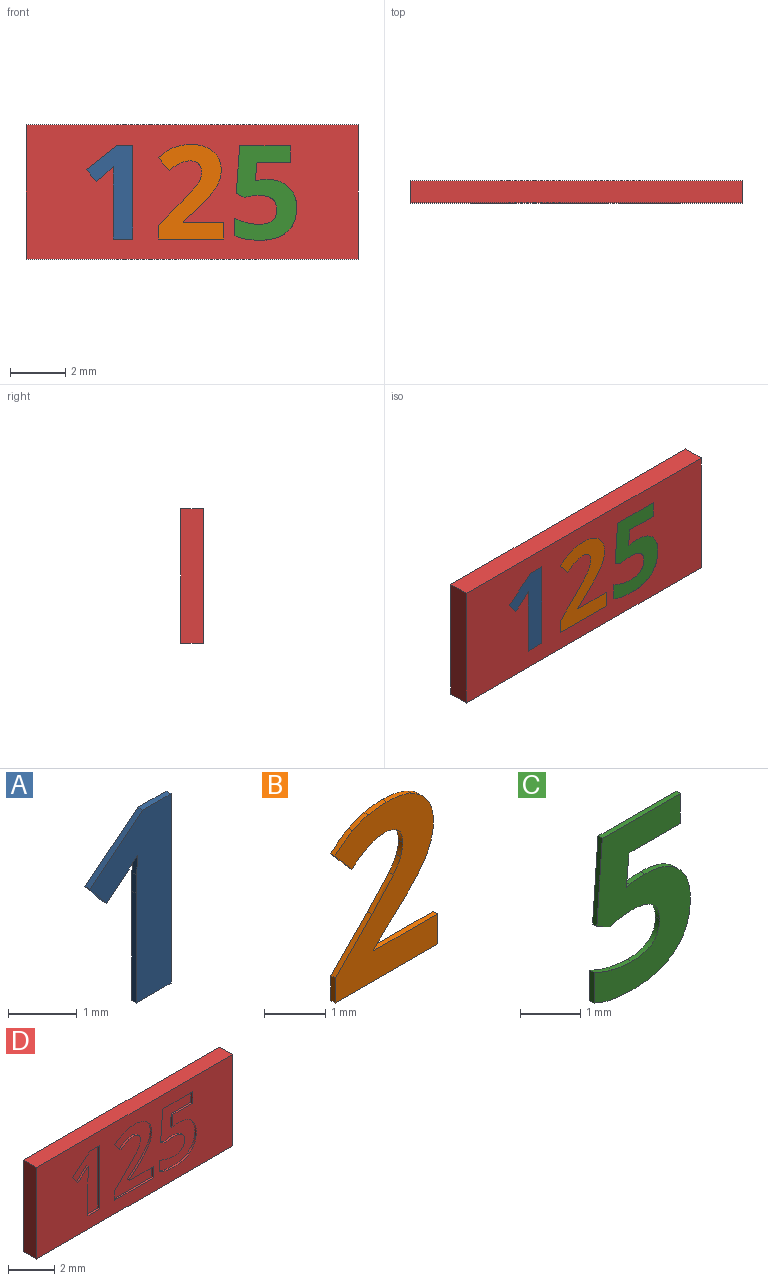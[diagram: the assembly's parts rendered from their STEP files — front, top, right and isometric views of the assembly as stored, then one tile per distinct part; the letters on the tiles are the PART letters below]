
ASSEMBLY  parts=4 mates=3
PART A: 12 faces, bbox 1.7x0.1x3.4 mm
  f0: plane 3.37x1.67mm, normal (0,-1,0), area 2.9mm2, adj f1,f2,f3,f4,f5,f6,f7,f9
  f1: plane 0.59x0.1mm, normal (0,0,1), area 0.1mm2, adj f0,f2,f8,f10
  f2: plane 1.09x0.86mm, normal (-0.62,0,0.78), area 0.1mm2, adj f0,f1,f3,f8
  f3: plane 0.43x0.34mm, normal (-0.78,0,-0.63), area 0.1mm2, adj f0,f2,f4,f8
  f4: plane 0.39x0.31mm, normal (0.63,0,-0.78), area 0mm2, adj f0,f3,f5,f8
  f5: extruded ~0.25x0.23mm, area 0mm2, adj f0,f4,f6,f8
  f6: plane 0.35x0.1mm, normal (-1,0,0.03), area 0mm2, adj f0,f5,f7,f8
  f7: plane 0.32x0.1mm, normal (-1,0,0.02), area 0mm2, adj f0,f6,f8,f9
  f8: plane 3.37x1.67mm, normal (0,1,0), area 2.9mm2, adj f1,f2,f3,f4,f5,f6,f7,f9
  f9: plane 1.95x0.1mm, normal (-1,0,0), area 0.2mm2, adj f0,f7,f8,f11
  f10: plane 3.37x0.1mm, normal (1,0,0), area 0.3mm2, adj f0,f1,f8,f11
  f11: plane 0.71x0.1mm, normal (0,0,-1), area 0.1mm2, adj f0,f8,f9,f10
PART B: 26 faces, bbox 2.4x0.1x3.4 mm
  f0: plane 3.42x2.37mm, normal (0,-1,0), area 4.2mm2, adj f1,f2,f3,f4,f5,f6,f7,f8
  f1: plane 1.47x0.1mm, normal (0,0,1), area 0.1mm2, adj f0,f2,f22,f24
  f2: plane 0.1x0.03mm, normal (1,0,0), area 0mm2, adj f0,f1,f3,f22
  f3: plane 0.43x0.41mm, normal (0.69,0,-0.73), area 0.1mm2, adj f0,f2,f4,f22
  f4: extruded ~0.61x0.61mm, area 0.1mm2, adj f0,f3,f5,f22
  f5: extruded ~0.42x0.25mm, area 0mm2, adj f0,f4,f6,f22
  f6: extruded ~0.44x0.1mm, area 0mm2, adj f0,f5,f7,f22
  f7: extruded ~0.48x0.13mm, area 0.1mm2, adj f0,f6,f8,f22
  f8: extruded ~0.38x0.32mm, area 0.1mm2, adj f0,f7,f9,f22
  f9: extruded ~0.56x0.12mm, area 0.1mm2, adj f0,f8,f10,f22
  f10: extruded ~0.43x0.1mm, area 0mm2, adj f0,f9,f11,f22
  f11: extruded ~0.36x0.13mm, area 0mm2, adj f0,f10,f12,f22
  f12: extruded ~0.41x0.3mm, area 0.1mm2, adj f0,f11,f13,f22
  f13: plane 0.46x0.39mm, normal (-0.76,0,-0.65), area 0.1mm2, adj f0,f12,f14,f22
  f14: extruded ~0.39x0.26mm, area 0mm2, adj f0,f13,f15,f22
  f15: extruded ~0.38x0.1mm, area 0mm2, adj f0,f14,f16,f22
  f16: extruded ~0.3x0.1mm, area 0mm2, adj f0,f15,f17,f22
  f17: extruded ~0.3x0.11mm, area 0mm2, adj f0,f16,f18,f22
  f18: extruded ~0.26x0.1mm, area 0mm2, adj f0,f17,f19,f22
  f19: extruded ~0.28x0.17mm, area 0mm2, adj f0,f18,f20,f22
  f20: extruded ~0.53x0.49mm, area 0.1mm2, adj f0,f19,f21,f22
  f21: plane 0.86x0.85mm, normal (-0.71,0,0.7), area 0.1mm2, adj f0,f20,f22,f23
  f22: plane 3.42x2.37mm, normal (0,1,0), area 4.2mm2, adj f1,f2,f3,f4,f5,f6,f7,f8
  f23: plane 0.5x0.1mm, normal (-1,0,0), area 0mm2, adj f0,f21,f22,f25
  f24: plane 0.6x0.1mm, normal (1,0,0), area 0.1mm2, adj f0,f1,f22,f25
  f25: plane 2.36x0.1mm, normal (0,0,-1), area 0.2mm2, adj f0,f22,f23,f24
PART C: 22 faces, bbox 2.3x0.1x3.4 mm
  f0: plane 3.42x2.25mm, normal (0,-1,0), area 4.5mm2, adj f1,f2,f3,f4,f5,f6,f7,f8
  f1: plane 0.1x0.08mm, normal (-0.2,0,0.98), area 0mm2, adj f0,f2,f18,f20
  f2: plane 0.66x0.1mm, normal (1,0,-0.09), area 0.1mm2, adj f0,f1,f3,f18
  f3: plane 1.2x0.1mm, normal (0,0,-1), area 0.1mm2, adj f0,f2,f4,f18
  f4: plane 0.6x0.1mm, normal (1,0,0), area 0.1mm2, adj f0,f3,f5,f18
  f5: plane 1.83x0.1mm, normal (0,0,1), area 0.2mm2, adj f0,f4,f6,f18
  f6: plane 1.72x0.13mm, normal (-1,0,0.07), area 0.2mm2, adj f0,f5,f7,f18
  f7: plane 0.28x0.15mm, normal (-0.47,0,-0.88), area 0mm2, adj f0,f6,f8,f18
  f8: extruded ~0.24x0.1mm, area 0mm2, adj f0,f7,f9,f18
  f9: extruded ~0.27x0.1mm, area 0mm2, adj f0,f8,f10,f18
  f10: extruded ~0.68x0.51mm, area 0.1mm2, adj f0,f9,f11,f18
  f11: extruded ~0.65x0.54mm, area 0.1mm2, adj f0,f10,f12,f18
  f12: extruded ~0.46x0.1mm, area 0mm2, adj f0,f11,f13,f18
  f13: extruded ~0.42x0.16mm, area 0mm2, adj f0,f12,f14,f18
  f14: plane 0.62x0.1mm, normal (-1,0,0), area 0.1mm2, adj f0,f13,f15,f18
  f15: extruded ~0.91x0.18mm, area 0.1mm2, adj f0,f14,f16,f18
  f16: extruded ~1x0.3mm, area 0.1mm2, adj f0,f15,f17,f18
  f17: extruded ~0.87x0.35mm, area 0.1mm2, adj f0,f16,f18,f19
  f18: plane 3.42x2.25mm, normal (0,1,0), area 4.5mm2, adj f1,f2,f3,f4,f5,f6,f7,f8
  f19: extruded ~0.75x0.29mm, area 0.1mm2, adj f0,f17,f18,f21
  f20: extruded ~0.35x0.1mm, area 0mm2, adj f0,f1,f18,f21
  f21: extruded ~0.78x0.27mm, area 0.1mm2, adj f0,f18,f19,f20
PART D: 63 faces, bbox 12x0.8x4.9 mm
  f0: plane 12x4.85mm, normal (0,-1,0), area 46.5mm2, adj f1,f2,f3,f4,f6,f7,f8,f9
  f1: plane 12x0.8mm, normal (0,0,-1), area 9.6mm2, adj f0,f2,f4,f5
  f2: plane 4.85x0.8mm, normal (1,0,0), area 3.9mm2, adj f0,f1,f3,f5
  f3: plane 12x0.8mm, normal (0,0,1), area 9.6mm2, adj f0,f2,f4,f5
  f4: plane 4.85x0.8mm, normal (-1,0,0), area 3.9mm2, adj f0,f1,f3,f5
  f5: plane 12x4.85mm, normal (0,1,0), area 58.2mm2, adj f1,f2,f3,f4
  f6: extruded ~0.35x0.1mm, area 0mm2, adj f0,f7,f25,f26
  f7: plane 0.1x0.08mm, normal (0.2,0,-0.98), area 0mm2, adj f0,f6,f8,f26
  f8: plane 0.66x0.1mm, normal (-1,0,0.09), area 0.1mm2, adj f0,f7,f9,f26
  f9: plane 1.2x0.1mm, normal (0,0,1), area 0.1mm2, adj f0,f8,f10,f26
  f10: plane 0.6x0.1mm, normal (-1,0,0), area 0.1mm2, adj f0,f9,f11,f26
  f11: plane 1.83x0.1mm, normal (0,0,-1), area 0.2mm2, adj f0,f10,f12,f26
  f12: plane 1.72x0.13mm, normal (1,0,-0.07), area 0.2mm2, adj f0,f11,f13,f26
  f13: plane 0.28x0.15mm, normal (0.47,0,0.88), area 0mm2, adj f0,f12,f14,f26
  f14: extruded ~0.24x0.1mm, area 0mm2, adj f0,f13,f15,f26
  f15: extruded ~0.27x0.1mm, area 0mm2, adj f0,f14,f16,f26
  f16: extruded ~0.68x0.51mm, area 0.1mm2, adj f0,f15,f17,f26
  f17: extruded ~0.65x0.54mm, area 0.1mm2, adj f0,f16,f18,f26
  f18: extruded ~0.46x0.1mm, area 0mm2, adj f0,f17,f19,f26
  f19: extruded ~0.42x0.16mm, area 0mm2, adj f0,f18,f20,f26
  f20: plane 0.62x0.1mm, normal (1,0,0), area 0.1mm2, adj f0,f19,f21,f26
  f21: extruded ~0.91x0.18mm, area 0.1mm2, adj f0,f20,f22,f26
  f22: extruded ~1x0.3mm, area 0.1mm2, adj f0,f21,f23,f26
  f23: extruded ~0.87x0.35mm, area 0.1mm2, adj f0,f22,f24,f26
  f24: extruded ~0.75x0.29mm, area 0.1mm2, adj f0,f23,f25,f26
  f25: extruded ~0.78x0.27mm, area 0.1mm2, adj f0,f6,f24,f26
  f26: plane 3.42x2.25mm, normal (0,-1,0), area 4.5mm2, adj f6,f7,f8,f9,f10,f11,f12,f13
  f27: plane 0.6x0.1mm, normal (-1,0,0), area 0.1mm2, adj f0,f28,f50,f51
  f28: plane 1.47x0.1mm, normal (0,0,-1), area 0.1mm2, adj f0,f27,f29,f51
  f29: plane 0.1x0.03mm, normal (-1,0,0), area 0mm2, adj f0,f28,f30,f51
  f30: plane 0.43x0.41mm, normal (-0.69,0,0.73), area 0.1mm2, adj f0,f29,f31,f51
  f31: extruded ~0.61x0.61mm, area 0.1mm2, adj f0,f30,f32,f51
  f32: extruded ~0.42x0.25mm, area 0mm2, adj f0,f31,f33,f51
  f33: extruded ~0.44x0.1mm, area 0mm2, adj f0,f32,f34,f51
  f34: extruded ~0.48x0.13mm, area 0.1mm2, adj f0,f33,f35,f51
  f35: extruded ~0.38x0.32mm, area 0.1mm2, adj f0,f34,f36,f51
  f36: extruded ~0.56x0.12mm, area 0.1mm2, adj f0,f35,f37,f51
  f37: extruded ~0.43x0.1mm, area 0mm2, adj f0,f36,f38,f51
  f38: extruded ~0.36x0.13mm, area 0mm2, adj f0,f37,f39,f51
  f39: extruded ~0.41x0.3mm, area 0.1mm2, adj f0,f38,f40,f51
  f40: plane 0.46x0.39mm, normal (0.76,0,0.65), area 0.1mm2, adj f0,f39,f41,f51
  f41: extruded ~0.39x0.26mm, area 0mm2, adj f0,f40,f42,f51
  f42: extruded ~0.38x0.1mm, area 0mm2, adj f0,f41,f43,f51
  f43: extruded ~0.3x0.1mm, area 0mm2, adj f0,f42,f44,f51
  f44: extruded ~0.3x0.11mm, area 0mm2, adj f0,f43,f45,f51
  f45: extruded ~0.26x0.1mm, area 0mm2, adj f0,f44,f46,f51
  f46: extruded ~0.28x0.17mm, area 0mm2, adj f0,f45,f47,f51
  f47: extruded ~0.53x0.49mm, area 0.1mm2, adj f0,f46,f48,f51
  f48: plane 0.86x0.85mm, normal (0.71,0,-0.7), area 0.1mm2, adj f0,f47,f49,f51
  f49: plane 0.5x0.1mm, normal (1,0,0), area 0mm2, adj f0,f48,f50,f51
  f50: plane 2.36x0.1mm, normal (0,0,1), area 0.2mm2, adj f0,f27,f49,f51
  f51: plane 3.42x2.37mm, normal (0,-1,0), area 4.2mm2, adj f27,f28,f29,f30,f31,f32,f33,f34
  f52: plane 3.37x0.1mm, normal (-1,0,0), area 0.3mm2, adj f0,f53,f61,f62
  f53: plane 0.59x0.1mm, normal (0,0,-1), area 0.1mm2, adj f0,f52,f54,f62
  f54: plane 1.09x0.86mm, normal (0.62,0,-0.78), area 0.1mm2, adj f0,f53,f55,f62
  f55: plane 0.43x0.34mm, normal (0.78,0,0.63), area 0.1mm2, adj f0,f54,f56,f62
  f56: plane 0.39x0.31mm, normal (-0.63,0,0.78), area 0mm2, adj f0,f55,f57,f62
  f57: extruded ~0.25x0.23mm, area 0mm2, adj f0,f56,f58,f62
  f58: plane 0.35x0.1mm, normal (1,0,-0.03), area 0mm2, adj f0,f57,f59,f62
  f59: plane 0.32x0.1mm, normal (1,0,-0.02), area 0mm2, adj f0,f58,f60,f62
  f60: plane 1.95x0.1mm, normal (1,0,0), area 0.2mm2, adj f0,f59,f61,f62
  f61: plane 0.71x0.1mm, normal (0,0,1), area 0.1mm2, adj f0,f52,f60,f62
  f62: plane 3.37x1.67mm, normal (0,-1,0), area 2.9mm2, adj f52,f53,f54,f55,f56,f57,f58,f59
PLACE A t=(-4.57,0.38,0)mm
PLACE B t=(-1.58,0.38,0)mm
PLACE C t=(1.09,0.38,0)mm
PLACE D t=(-0.04,0.38,0)mm
MATE fastened A.f0 <-> D.f0  axis (0,-1,0) through (-2.89,-0.42,-1.7)mm
MATE fastened C.f0 <-> D.f0  axis (0,-1,0) through (1.49,-0.42,-1.56)mm
MATE fastened B.f0 <-> D.f0  axis (0,-1,0) through (-1.25,-0.42,-1.7)mm
